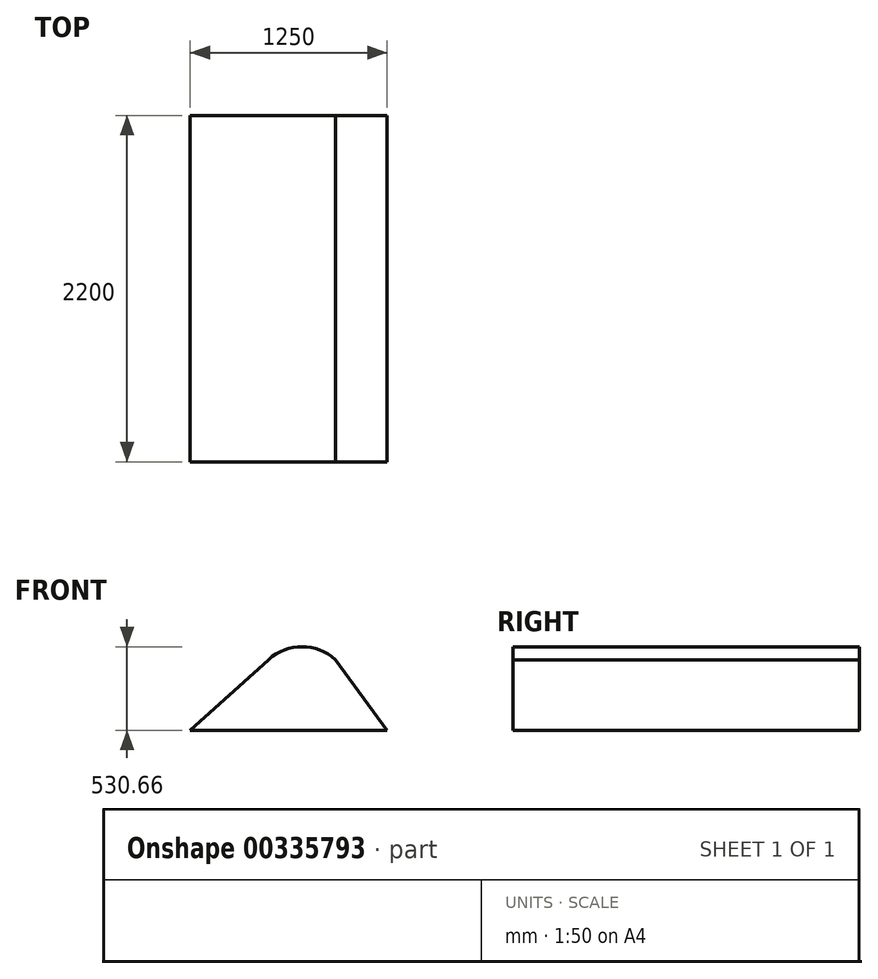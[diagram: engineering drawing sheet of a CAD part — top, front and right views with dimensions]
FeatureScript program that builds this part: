
annotation { "Feature Type Name" : "Feature", "Feature Type Description" : "" }
export const myFeature = defineFeature(function(context is Context, id is Id, definition is map)
    precondition{}
    {
        {
            var Q0;
            Q0=qCreatedBy(makeId("Front.planeOp"),FACE);
            var sketch = newSketch(context, id + "F0", { "sketchPlane" : qUnion([Q0])});
            skArc(sketch, "E0", {"start": v(-212.3, 449.1) * mm, "mid": v(0, 530.66) * mm, "end": v(212.3, 449.1) * mm});
            skLineSegment(sketch, "E1", {"start": v(-212.3, 449.1) * mm, "end": v(-710.5, 0) * mm});
            skLineSegment(sketch, "E2", {"start": v(-710.5, 0) * mm, "end": v(539.5, 0) * mm});
            skLineSegment(sketch, "E3", {"start": v(539.5, 0) * mm, "end": v(212.3, 449.1) * mm});
            skLineSegment(sketch, "E4", {"start": v(-212.3, 449.1) * mm, "end": v(212.3, 449.1) * mm, "construction": true});
            skLineSegment(sketch, "E5", {"start": v(-755.48, 530.66) * mm, "end": v(595.9, 530.66) * mm, "construction": true});
            skLineSegment(sketch, "E6", {"start": v(0, 0) * mm, "end": v(0, 852.36) * mm, "construction": true});
            skSolve(sketch);
        }
        {
            var Q0;
            Q0 = qSketchRegion(id + "F0", true);
            extrude(context, id + "F1", {"entities" : qUnion([Q0]), "endBound" : BoundingType.SYMMETRIC, "depth" : 2200 * mm});
        }
    });
